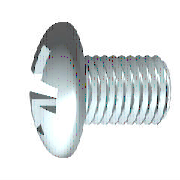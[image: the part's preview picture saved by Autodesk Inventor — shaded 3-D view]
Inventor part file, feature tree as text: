
AUTODESK INVENTOR PART (.ipt)
format: ipt  version: 2020 (Build 240168000, 168)  size: 276,480 bytes
history: native  units: mm (DEFAULTED — no unit token found)
features: other x2, plane x2, extrude x1
ambient origin geometry x7: Origin, YZ Plane, XZ Plane, X Axis, Y Axis, Z Axis, Center Point
bodies: Solid1 (feature_tree)
feature tree (5):
  other  "Базовый элемент"
  plane  "Work Plane1"
  extrude  "Паз"  Depth=1.6mm
  other  "Вырез"
  plane  "Work Plane3"
